# Revit family: Medical_All_Hill-Rom_Connex-Spot-Monitor
name_source: partatom
category: Specialty Equipment
revit_build: Autodesk Revit Architecture 2015 (Build: 20140606_1530(x64)
units: mm (PartAtom-declared; Revit-internal decimal feet)

## types (1)
- CSM - Connex Spot Monitor
    Ambient Temperature = 50 – 104°F / 10 - 40°C
    BIMobject category = All
    BIMobject category code = medical-all
    BIMobject main category = Medical
    BIMobject main category code = medical
    Battery Recharge Time = 4 Hours
    Brand url = https://construction.hill-rom.com
    Depth = 6.00"
    Description = The Connex® Spot Monitor features an easy-to-use, vivid touchscreen display and provides accurate vital signs measurement including blood pressure averaging, spot checking, interval monitoring and custom scoring across patient populations. The device connects wirelessly to your EMR and sends vitals to the patient chart from the point of care to help improve efficiency.
    Design country = United States
    Edition number = 1
    Full Load Current = 2 A
    Height = 10.00"
    Installation instructions = https://construction.hill-rom.com
    Manufacturer = Hill-Rom
    Manufacturer country = United States
    Manufacturer name = Hill-Rom
    Masterformat 2014 Code = 11 70 00
    Masterformat 2014 Description = Healthcare Equipment
    Max Amperage = 0 A
    Model = Connex Spot Monitor
    Monitor material = Plastic-Hill-Rom-White
    NBS Reference Code = 75-50
    NBS Reference Description = Medical Safety Systems
    Nominal height = 0.00"
    Nominal width = 0.00"
    OmniClass Code = 23-25 00 00
    OmniClass Description = Medical and Laboratory Equipment
    Operating Time (APM with 9-Cell Battery) = Up to 17 hours
    Operating Time (Integrated 2-Cell Battery) = Up to 12 hours with fully charged battery (6 patients per device, vitals every 4 hours with NIPB, SpO2, temp, WiFi and barcode scan)
    Power Factor = 1
    Product Guid = da2055e0-8f79-4f45-8312-7ce0dd7982e7
    Product SKU = WelchAllyn-ConnexSpotMonitor
    Product data url = https://bimobject.com
    Product family = Vital Signs Monitoring
    Product group = CSM
    Product url = https://www.welchallyn.com
    QR code = http://bimobject.com
    Relative humidity = 15% - 90 %
    Screen material = Glass-Hill-Rom-Display
    Technical description = https://construction.hill-rom.com
    URL = https://www.hill-rom.com
    Uniclass 1.4 Code = L852
    Uniclass 1.4 Description = Medical furniture, fittings
    Uniclass 2.0 Code = SS-75-50
    Uniclass 2.0 Description = Medical Safety Systems
    Uniclass 2015 Code = Pr_40_70_51
    Uniclass 2015 Name = Medical and laboratory equipment
    Voltage = 15 V
    Weight = 9.50 lbm
    Weight Net (Kg) = 0
    Wheels material = Plastic-Hill-Rom-Black
    Width = 11.00"
    Youtube clip = https://www.youtube.com

## geometry (parser evidence)
native form markers: Blend x4, Sweep x3
no freeform markers — native parametric forms only
